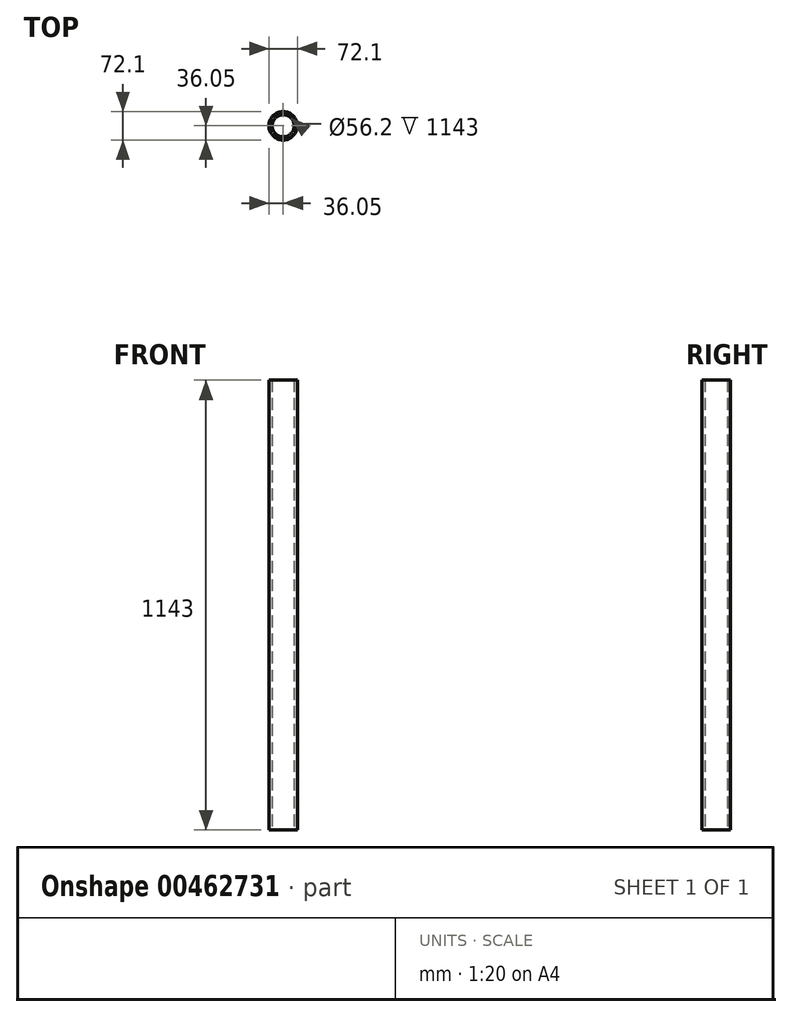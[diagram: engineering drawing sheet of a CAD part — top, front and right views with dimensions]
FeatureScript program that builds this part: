
annotation { "Feature Type Name" : "Feature", "Feature Type Description" : "" }
export const myFeature = defineFeature(function(context is Context, id is Id, definition is map)
    precondition{}
    {
        {
            var Q0;
            Q0=qCreatedBy(makeId("Top.planeOp"),FACE);
            var sketch = newSketch(context, id + "F0", { "sketchPlane" : qUnion([Q0])});
            skCircle(sketch, "E0", {"center": v(0, 0) * mm, "radius": 36.05 * mm});
            skCircle(sketch, "E1", {"center": v(0, 0) * mm, "radius": 28.1 * mm});
            skSolve(sketch);
        }
        {
            var Q0;
            Q0=makeQuery(id+"F0.imprint","IMPRINT",FACE,{"disambiguationData":[TD([[makeQuery(id+"F0.imprint","IMPRINT",EDGE,{"derivedFrom":sQuery(id+"F0.wireOp",EDGE,"E0")}),1.0]])]});
            extrude(context, id + "F1", {"entities" : qUnion([Q0]), "depth" : 1143 * mm});
        }
    });
